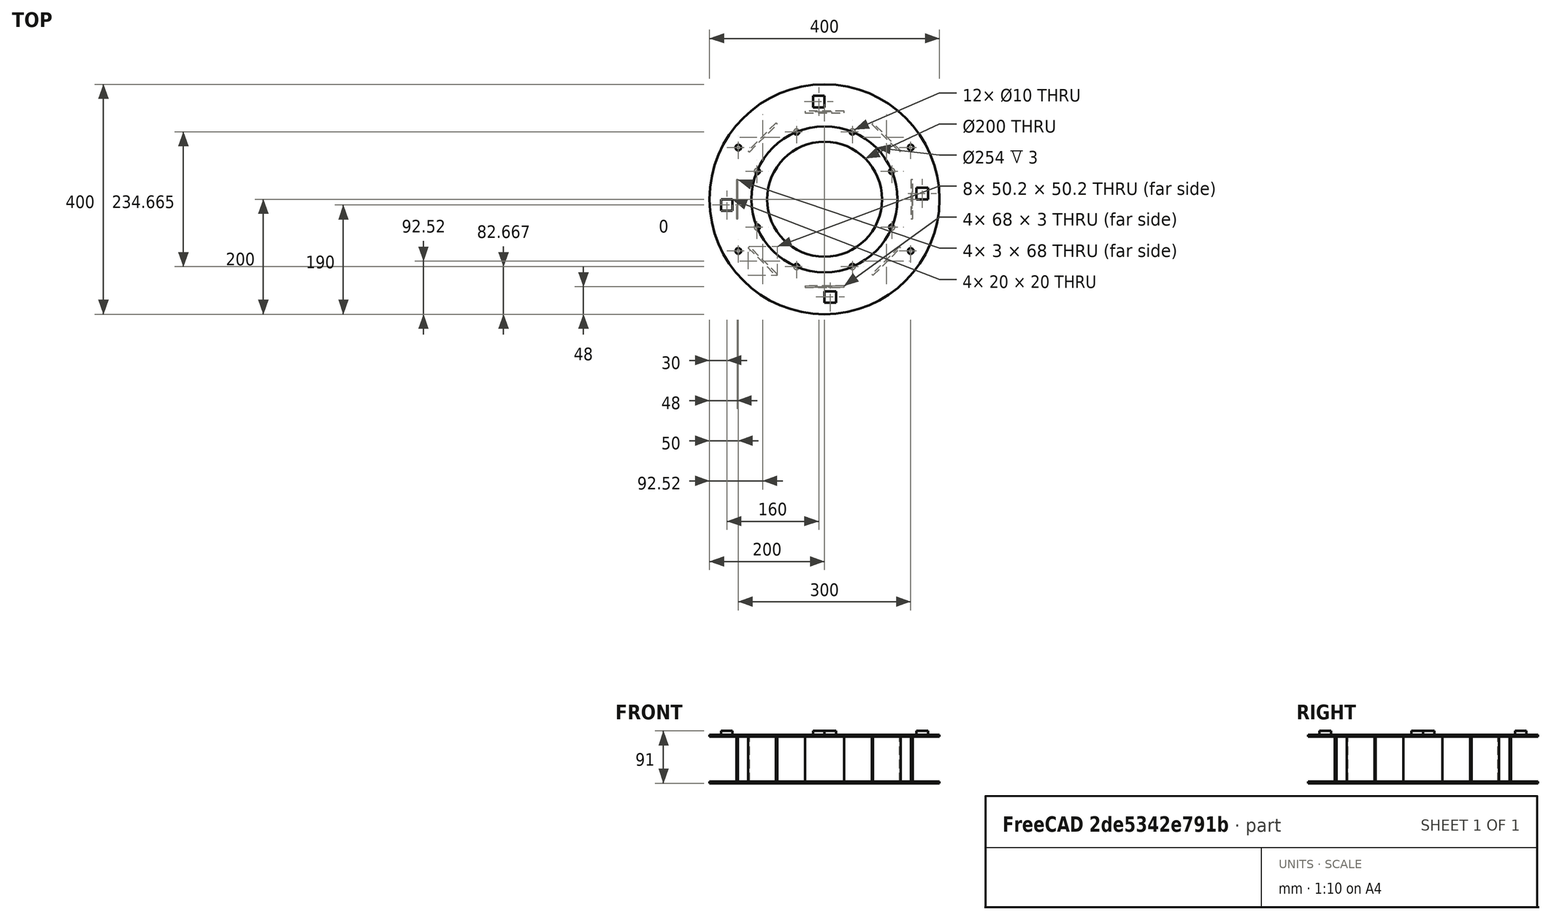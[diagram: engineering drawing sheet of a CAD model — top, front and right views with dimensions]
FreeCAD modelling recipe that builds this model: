
FCSTD DOCUMENT  (FreeCAD 0.21R33771 (Git))
Label: FEA_Model_MM
License: Creative Commons Attribution-ShareAlike 4.0
LicenseURL: https://creativecommons.org/licenses/by-sa/4.0/
objects: Sketcher::SketchObject×4, PartDesign::Pad×4, Fem::ConstraintForce×4, Fem::FemMeshObjectPython×2, PartDesign::Plane×1, PartDesign::PolarPattern×1, PartDesign::MultiTransform×1, App::MaterialObjectPython×1, Fem::ConstraintFixed×1, PartDesign::Body×1, Fem::FemSolverObjectPython×1, Fem::FemResultObjectPython×1, Fem::FemPostWarpVectorFilter×1, Fem::FemPostPipeline×1, Fem::FemAnalysis×1
note: 16 computed .brp shape members not serialized (recipe doc carries the construction recipe); baked Part::Feature solids carry a one-line shape summary decoded from their .brp

FEATURE [Sketcher::SketchObject] Sketch
  FullyConstrained = true
  MapMode = 5
  Support = -> [XY_Plane]
  sketch-geometry (19):
    g0: Circle CenterX=0 CenterY=0 CenterZ=0 NormalX=0 NormalY=0 NormalZ=1 AngleXU=0 Radius=100
    g1: Circle CenterX=0 CenterY=0 CenterZ=0 NormalX=0 NormalY=0 NormalZ=1 AngleXU=0 Radius=200
    g2: LineSegment StartX=-117.333 StartY=48.6008 StartZ=0 EndX=-117.333 EndY=-48.6008 EndZ=0
    g3: LineSegment StartX=-117.333 StartY=-48.6008 StartZ=0 EndX=-48.6008 EndY=-117.333 EndZ=0
    g4: LineSegment StartX=-48.6008 StartY=-117.333 StartZ=0 EndX=48.6008 EndY=-117.333 EndZ=0
    g5: LineSegment StartX=48.6008 StartY=-117.333 StartZ=0 EndX=117.333 EndY=-48.6008 EndZ=0
    g6: LineSegment StartX=117.333 StartY=-48.6008 StartZ=0 EndX=117.333 EndY=48.6008 EndZ=0
    g7: LineSegment StartX=117.333 StartY=48.6008 StartZ=0 EndX=48.6008 EndY=117.333 EndZ=0
    g8: LineSegment StartX=48.6008 StartY=117.333 StartZ=0 EndX=-48.6008 EndY=117.333 EndZ=0
    g9: LineSegment StartX=-48.6008 StartY=117.333 StartZ=0 EndX=-117.333 EndY=48.6008 EndZ=0
    g10: Circle CenterX=0 CenterY=0 CenterZ=0 NormalX=0 NormalY=0 NormalZ=1 AngleXU=0 Radius=127
    g11: Circle CenterX=-117.333 CenterY=48.6008 CenterZ=0 NormalX=0 NormalY=0 NormalZ=1 AngleXU=0 Radius=5
    g12: Circle CenterX=-48.6008 CenterY=117.333 CenterZ=0 NormalX=0 NormalY=0 NormalZ=1 AngleXU=0 Radius=5
    g13: Circle CenterX=48.6008 CenterY=117.333 CenterZ=0 NormalX=0 NormalY=0 NormalZ=1 AngleXU=0 Radius=5
    g14: Circle CenterX=117.333 CenterY=48.6008 CenterZ=0 NormalX=0 NormalY=0 NormalZ=1 AngleXU=0 Radius=5
    g15: Circle CenterX=117.333 CenterY=-48.6008 CenterZ=0 NormalX=0 NormalY=0 NormalZ=1 AngleXU=0 Radius=5
    g16: Circle CenterX=48.6008 CenterY=-117.333 CenterZ=0 NormalX=0 NormalY=0 NormalZ=1 AngleXU=0 Radius=5
    g17: Circle CenterX=-48.6008 CenterY=-117.333 CenterZ=0 NormalX=0 NormalY=0 NormalZ=1 AngleXU=0 Radius=5
    g18: Circle CenterX=-117.333 CenterY=-48.6008 CenterZ=0 NormalX=0 NormalY=0 NormalZ=1 AngleXU=0 Radius=5
  constraints (40):
    c: Coincident(g0,g-1)
    c: Coincident(g1,g0)
    c: Diameter(g1) = 400
    c: Diameter(g0) = 200
    c: Coincident(g2,g3)
    c: Coincident(g3,g4)
    c: Coincident(g4,g5)
    c: Coincident(g5,g6)
    c: Coincident(g6,g7)
    c: Coincident(g7,g8)
    c: Coincident(g8,g9)
    c: Coincident(g9,g2)
    c: Equal(g2, g3-g9) x7
    c: PointOnObject(g2,g10)
    c: PointOnObject(g3,g10)
    c: PointOnObject(g4,g10)
    c: PointOnObject(g5,g10)
    c: PointOnObject(g6,g10)
    c: PointOnObject(g7,g10)
    c: PointOnObject(g8,g10)
    c: PointOnObject(g9,g10)
    c: Coincident(g10,g0)
    c: Vertical(g2)
    c: Diameter(g10) = 254
    c: Coincident(g11,g2)
    c: Diameter(g11) = 10
    c: Equal(g11,g12) = 10
    c: Coincident(g12,g8)
    c: Coincident(g13,g7)
    c: Equal(g13,g11)
    c: Coincident(g14,g6)
    c: Coincident(g15,g5)
    c: Coincident(g16,g4)
    c: Coincident(g17,g3)
    c: Coincident(g18,g2)
    c: Equal(g14,g15)
    c: Equal(g15,g16)
    c: Equal(g16,g17)
    c: Equal(g17,g18)
    c: Equal(g18,g11)
FEATURE [PartDesign::Pad] Pad
  Direction = (0,0,1)
  Length = 3
  Length2 = 10
  Profile = -> Sketch
  ReferenceAxis = -> Sketch [N_Axis]
  Type = 0
FEATURE [Sketcher::SketchObject] Sketch001
  FullyConstrained = true
  MapMode = 5
  Support = -> [XY_Plane]
  sketch-geometry (7):
    g0: LineSegment StartX=-153.5 StartY=34 StartZ=0 EndX=-150.5 EndY=34 EndZ=0
    g1: LineSegment StartX=-150.5 StartY=34 StartZ=0 EndX=-150.5 EndY=-34 EndZ=0
    g2: LineSegment StartX=-150.5 StartY=-34 StartZ=0 EndX=-153.5 EndY=-34 EndZ=0
    g3: LineSegment StartX=-153.5 StartY=-34 StartZ=0 EndX=-153.5 EndY=34 EndZ=0
    g4: LineSegment StartX=-153.5 StartY=34 StartZ=0 EndX=-150.5 EndY=-34 EndZ=0
    g5: LineSegment StartX=-153.5 StartY=-34 StartZ=0 EndX=-150.5 EndY=34 EndZ=0
    g6: GeomPoint X=-152 Y=0 Z=0
  constraints (18):
    c: Coincident(g0,g1)
    c: Coincident(g1,g2)
    c: Coincident(g2,g3)
    c: Coincident(g3,g0)
    c: Horizontal(g0)
    c: Horizontal(g2)
    c: Vertical(g1)
    c: Vertical(g3)
    c: DistanceY(g3,g3) = 68
    c: DistanceX(g0,g0) = 3
    c: Coincident(g4,g0)
    c: Coincident(g4,g1)
    c: Coincident(g5,g2)
    c: Coincident(g5,g0)
    c: PointOnObject(g6,g4)
    c: PointOnObject(g6,g5)
    c: DistanceX(g6,g-1) = 152
    c: PointOnObject(g6,g-1)
FEATURE [PartDesign::Pad] Pad001
  BaseFeature = -> Pad
  Direction = (0,0,1)
  Length = 84
  Length2 = 10
  Profile = -> Sketch001
  ReferenceAxis = -> Sketch001 [N_Axis]
  Type = 0
FEATURE [PartDesign::Plane] DatumPlane
  AttachmentOffset = pos=(0,0,81) rot=(0,0,1;0rad)
  Length = 479.171
  MapMode = 5
  Placement = pos=(0,0,81) rot=(0,0,1;0rad)
  ResizeMode = 0
  Support = -> [XY_Plane]
  Width = 479.531
FEATURE [Sketcher::SketchObject] Sketch002
  FullyConstrained = true
  MapMode = 5
  Placement = pos=(0,0,81) rot=(0,0,1;0rad)
  Support = -> [DatumPlane]
  sketch-geometry (11):
    g0: Circle CenterX=0 CenterY=0 CenterZ=0 NormalX=0 NormalY=0 NormalZ=1 AngleXU=0 Radius=200
    g1: Circle CenterX=0 CenterY=0 CenterZ=0 NormalX=0 NormalY=0 NormalZ=1 AngleXU=0 Radius=127
    g2: Circle CenterX=-150 CenterY=90 CenterZ=0 NormalX=0 NormalY=0 NormalZ=1 AngleXU=0 Radius=5
    g3: Circle CenterX=-150 CenterY=-90 CenterZ=0 NormalX=0 NormalY=0 NormalZ=1 AngleXU=0 Radius=5
    g4: Circle CenterX=150 CenterY=90 CenterZ=0 NormalX=0 NormalY=0 NormalZ=1 AngleXU=0 Radius=5
    g5: Circle CenterX=150 CenterY=-90 CenterZ=0 NormalX=0 NormalY=0 NormalZ=1 AngleXU=0 Radius=5
    g6: LineSegment StartX=150 StartY=-90 StartZ=0 EndX=150 EndY=90 EndZ=0
    g7: LineSegment StartX=150 StartY=90 StartZ=0 EndX=-150 EndY=90 EndZ=0
    g8: LineSegment StartX=-150 StartY=90 StartZ=0 EndX=-150 EndY=-90 EndZ=0
    g9: LineSegment StartX=-150 StartY=-90 StartZ=0 EndX=150 EndY=-90 EndZ=0
    g10: GeomPoint X=0 Y=0 Z=0
  constraints (24):
    c: Diameter(g0) = 400
    c: Coincident(g1,g-1)
    c: Diameter(g1) = 254
    c: Coincident(g0,g1)
    c: Coincident(g6,g7)
    c: Coincident(g7,g8)
    c: Coincident(g8,g9)
    c: Coincident(g9,g6)
    c: Horizontal(g7)
    c: Horizontal(g9)
    c: Vertical(g6)
    c: Vertical(g8)
    c: Symmetric(g7,g6,g10)
    c: Coincident(g10,g0)
    c: Coincident(g7,g2)
    c: Coincident(g4,g6)
    c: Coincident(g5,g6)
    c: Coincident(g3,g8)
    c: Equal(g2,g4)
    c: Equal(g4,g5)
    c: Equal(g5,g3)
    c: Diameter(g2) = 10
    c: DistanceY(g8,g8) = 180
    c: DistanceX(g7,g7) = 300
FEATURE [PartDesign::Pad] Pad002
  BaseFeature = -> Pad001
  Direction = (0,0,1)
  Length = 3
  Length2 = 10
  Profile = -> Sketch002
  ReferenceAxis = -> Sketch002 [N_Axis]
  Type = 0
FEATURE [PartDesign::PolarPattern] PolarPattern
  Angle = 360
  Axis = -> Sketch001 [N_Axis]
  Occurrences = 8
FEATURE [PartDesign::MultiTransform] MultiTransform
  BaseFeature = -> Pad002
  Originals = -> [Pad001]
  Transformations = -> [PolarPattern]
FEATURE [App::MaterialObjectPython] MaterialSolid  # material (typed FeaturePython)
  Category = 0
  Material = AuthorAndLicense=(c) 2013 Juergen Riegel (CC-BY 3.0),CardName=Steel-Generic,Density=7900 kg/m^3,+9 more (map truncated)
FEATURE [Fem::ConstraintFixed] ConstraintFixed
  NormalDirection = (1,-1e-16,0)
  Normals = (96) [(-1,0,0),(0.5,-0.866025,0),(0.5,0.866025,0),(-1,2.44929e-16,0),(-1,0,0),(0.5,-0.866025,0),(0.5,0.866025,0),(-1,2.44929e-16,0),(-1,0,0),+87 more]
  Points = (96) [(122.333,-48.6008,3),(114.833,-44.2707,3),(114.833,-52.9309,3),(122.333,-48.6008,3),(122.333,-48.6008,1.5),(114.833,-44.2707,1.5),+90 more]
  References = -> [MultiTransform]
  Scale = 2
FEATURE [Sketcher::SketchObject] Sketch003
  FullyConstrained = true
  MapMode = 5
  Placement = pos=(0,0,81) rot=(0,0,1;0rad)
  Support = -> [DatumPlane]
  sketch-geometry (20):
    g0: LineSegment StartX=160 StartY=20 StartZ=0 EndX=160 EndY=0 EndZ=0
    g1: LineSegment StartX=160 StartY=0 StartZ=0 EndX=180 EndY=0 EndZ=0
    g2: LineSegment StartX=180 StartY=0 StartZ=0 EndX=180 EndY=20 EndZ=0
    g3: LineSegment StartX=180 StartY=20 StartZ=0 EndX=160 EndY=20 EndZ=0
    g4: GeomPoint X=170 Y=10 Z=0
    g5: LineSegment StartX=-20 StartY=180 StartZ=0 EndX=-20 EndY=160 EndZ=0
    g6: LineSegment StartX=-20 StartY=160 StartZ=0 EndX=0 EndY=160 EndZ=0
    g7: LineSegment StartX=0 StartY=160 StartZ=0 EndX=0 EndY=180 EndZ=0
    g8: LineSegment StartX=0 StartY=180 StartZ=0 EndX=-20 EndY=180 EndZ=0
    g9: GeomPoint X=-10 Y=170 Z=0
    g10: LineSegment StartX=-180 StartY=0 StartZ=0 EndX=-180 EndY=-20 EndZ=0
    g11: LineSegment StartX=-180 StartY=-20 StartZ=0 EndX=-160 EndY=-20 EndZ=0
    g12: LineSegment StartX=-160 StartY=-20 StartZ=0 EndX=-160 EndY=0 EndZ=0
    g13: LineSegment StartX=-160 StartY=0 StartZ=0 EndX=-180 EndY=0 EndZ=0
    g14: GeomPoint X=-170 Y=-10 Z=0
    g15: LineSegment StartX=0 StartY=-160 StartZ=0 EndX=0 EndY=-180 EndZ=0
    g16: LineSegment StartX=0 StartY=-180 StartZ=0 EndX=20 EndY=-180 EndZ=0
    g17: LineSegment StartX=20 StartY=-180 StartZ=0 EndX=20 EndY=-160 EndZ=0
    g18: LineSegment StartX=20 StartY=-160 StartZ=0 EndX=0 EndY=-160 EndZ=0
    g19: GeomPoint X=10 Y=-170 Z=0
  constraints (52):
    c: Coincident(g0,g1)
    c: Coincident(g1,g2)
    c: Coincident(g2,g3)
    c: Coincident(g3,g0)
    c: Horizontal(g1)
    c: Horizontal(g3)
    c: Vertical(g0)
    c: Vertical(g2)
    c: Symmetric(g1,g0,g4)
    c: Coincident(g5,g6)
    c: Coincident(g6,g7)
    c: Coincident(g7,g8)
    c: Coincident(g8,g5)
    c: Horizontal(g6)
    c: Horizontal(g8)
    c: Vertical(g5)
    c: Vertical(g7)
    c: Symmetric(g6,g5,g9)
    c: Coincident(g10,g11)
    c: Coincident(g11,g12)
    c: Coincident(g12,g13)
    c: Coincident(g13,g10)
    c: Horizontal(g11)
    c: Horizontal(g13)
    c: Vertical(g10)
    c: Vertical(g12)
    c: Symmetric(g11,g10,g14)
    c: Coincident(g15,g16)
    c: Coincident(g16,g17)
    c: Coincident(g17,g18)
    c: Coincident(g18,g15)
    c: Horizontal(g16)
    c: Horizontal(g18)
    c: Vertical(g15)
    c: Vertical(g17)
    c: Symmetric(g16,g15,g19)
    c: DistanceX(g16,g16) = 20
    c: PointOnObject(g15,g-2)
    c: Equal(g17,g18)
    c: DistanceY(g19,g-1) = 170
    c: DistanceY(g-1,g9) = 170
    c: DistanceX(g-1,g4) = 170
    c: DistanceX(g14,g-1) = 170
    c: Equal(g18,g13)
    c: Equal(g13,g12)
    c: Equal(g12,g6)
    c: Equal(g6,g7)
    c: Equal(g7,g3)
    c: Equal(g3,g2)
    c: PointOnObject(g12,g-1)
    c: PointOnObject(g0,g-1)
    c: PointOnObject(g6,g-2)
FEATURE [PartDesign::Pad] Pad003
  BaseFeature = -> MultiTransform
  Direction = (0,0,1)
  Length = 10
  Length2 = 10
  Profile = -> Sketch003
  ReferenceAxis = -> Sketch003 [N_Axis]
  Type = 0
FEATURE [PartDesign::Body] Body
  Group = -> [Sketch,Pad,Sketch001,Pad001,DatumPlane,Sketch002,Pad002,MultiTransform,PolarPattern,Sketch003,Pad003]
  Origin = -> Origin
  Tip = -> Pad003
FEATURE [Fem::ConstraintForce] ConstraintForce
  Direction = -> Pad003 [Face80]
  DirectionVector = (-1,0,0)
  Force = 2860
  NormalDirection = (1,0,0)
  Points = (9) [(0,160,91),(0,170,91),(0,180,91),(0,160,87.5),(0,170,87.5),(0,180,87.5),(0,160,84),(0,170,84),(0,180,84)]
  References = -> [Pad003]
FEATURE [Fem::ConstraintForce] ConstraintForce001
  Direction = -> Pad003 [Face69]
  DirectionVector = (0,-1,0)
  Force = 2860
  NormalDirection = (0,1,0)
  Points = (9) [(-160,-1.8434e-27,91),(-170,-1.8434e-27,91),(-180,-1.8434e-27,91),(-160,-1.8434e-27,87.5),(-170,-1.8434e-27,87.5),(-180,-1.8434e-27,87.5),+3 more]
  References = -> [Pad003]
FEATURE [Fem::ConstraintForce] ConstraintForce002
  Direction = -> Pad003 [Face74]
  DirectionVector = (1,0,0)
  Force = 2860
  NormalDirection = (-1,0,0)
  Points = (9) [(0,-160,91),(0,-170,91),(0,-180,91),(0,-160,87.5),(0,-170,87.5),(0,-180,87.5),(0,-160,84),(0,-170,84),(0,-180,84)]
  References = -> [Pad003]
FEATURE [Fem::ConstraintForce] ConstraintForce003
  Direction = -> Pad003 [Face83]
  DirectionVector = (0,1,0)
  Force = 2860
  NormalDirection = (0,-1,0)
  Points = (9) [(160,0,91),(170,0,91),(180,0,91),(160,0,87.5),(170,0,87.5),(180,0,87.5),(160,0,84),(170,0,84),(180,0,84)]
  References = -> [Pad003]
FEATURE [Fem::FemMeshObjectPython] FEMMeshGmsh  # FEM object (typed FeaturePython)
  Algorithm2D = 0
  Algorithm3D = 0
  CharacteristicLengthMax = 0
  CharacteristicLengthMin = 0
  CoherenceMesh = true
  ElementDimension = 0
  ElementOrder = 1
  GeometryTolerance = 1e-06
  GroupsOfNodes = false
  HighOrderOptimize = 0
  MeshSizeFromCurvature = 12
  OptimizeNetgen = false
  OptimizeStd = true
  Part = -> Pad003
  RecombinationAlgorithm = 0
  Recombine3DAll = false
  RecombineAll = false
  SecondOrderLinear = false
FEATURE [Fem::FemSolverObjectPython] SolverCalculix  # FEM object (typed FeaturePython)
  AnalysisType = 0
  BeamShellResultOutput3D = false
  BucklingFactors = 1
  EigenmodeHighLimit = 1000000
  EigenmodeLowLimit = 0
  EigenmodesCount = 10
  GeometricalNonlinearity = 0
  IterationsControlParameterCutb = 0.25,0.5,0.75,0.85,,,1.5,
  IterationsControlParameterIter = 4,8,9,200,10,400,,200,,
  IterationsControlParameterTimeUse = false
  IterationsThermoMechMaximum = 200
  IterationsUserDefinedIncrementations = false
  IterationsUserDefinedTimeStepLength = false
  MaterialNonlinearity = 0
  MatrixSolverType = 0
  SplitInputWriter = false
  ThermoMechSteadyState = true
  TimeEnd = 1
  TimeInitialStep = 1
FEATURE [Fem::FemMeshObjectPython] CalculiX_static_Results_Mesh  # FEM object (typed FeaturePython)
FEATURE [Fem::FemResultObjectPython] CalculiX_static_Results  # FEM object (typed FeaturePython)
  DisplacementLengths = [0.00443829,0.00948363,0.0531553,0.059592,0.0527868,0.0598505,0,0.0567763,0.0559713,0.0553691,0.0547576,0,0,0.0599348,0.0524196,0.0605346,0.0524333,0.00102122,0,0.0583304,0.0612851,0.0566849,0.0593827,0.0597518,0.0598739,0.0579958,0.0580854,+9944 more]
  DisplacementVectors = (9971) [(7.31591e-05,-0.00121443,0.00426828),(-0.000139388,0.0084701,0.00426348),(0.00177561,-0.000946487,-0.0531172),(0.00122495,-0.00164273,0.0595568),+9967 more]
  Eigenmode = 0
  EigenmodeFrequency = 0
  MaxShear = [2.86889,4.14064,26.6509,22.8504,33.4617,29.1717,38.147,38.7939,27.3453,29.3922,34.469,15.7311,75.7877,22.3645,35.0224,27.7075,45.6999,4.89391,72.4257,33.7964,34.082,29.3256,41.9173,42.3489,31.2234,34.9488,38.3984,13.9466,32.8553,32.0148,+9941 more]
  Mesh = -> CalculiX_static_Results_Mesh
  NodeNumbers = [1,2,3,4,5,6,7,8,9,10,11,12,13,14,15,16,17,18,19,20,21,22,23,24,25,26,27,28,29,30,31,32,33,34,35,36,37,38,39,40,41,42,43,44,45,46,47,48,49,50,51,52,53,54,55,56,57,58,59,60,61,62,63,64,65,66,67,68,69,+9902 more]
  NodeStrainXX = [2.89428e-06,2.9041e-06,0.000104244,-0.000127983,0.000239446,-0.000182598,0.000370822,0.000319939,-0.000232457,0.000237146,-0.000271771,9.57066e-05,0.000824076,0.000147686,-0.000158657,0.000183865,-0.000274726,-1.26717e-05,0.000447431,+9952 more]
  NodeStrainXY = [-7.32097e-06,5.97958e-06,-7.80433e-05,6.0767e-05,-2.5812e-05,-1.92927e-05,-0.000119813,-2.32105e-05,1.39353e-05,1.42495e-05,1.68466e-05,-8.68847e-05,-1.78014e-05,5.6663e-05,-0.000121466,-3.48939e-06,-9.62688e-06,-3.08973e-05,0.000367249,+9952 more]
  NodeStrainXZ = [1.3202e-06,-1.36864e-06,-5.23125e-05,3.86446e-05,-2.26082e-05,2.30176e-05,0.000109802,-6.58045e-06,-1.77337e-05,2.78298e-05,4.24475e-05,2.23947e-05,0.000270543,4.80188e-05,-5.20292e-05,5.5632e-05,-4.06931e-06,-5.32338e-06,0.000178004,+9952 more]
  NodeStrainYY = [2.29075e-05,3.33936e-05,0.000174772,-0.000114426,0.000224883,-0.000218856,2.95276e-06,0.000149745,-9.57722e-05,0.000164125,-0.00020956,-1.53717e-06,3.56518e-06,0.000103975,-0.000199856,0.000182289,-0.000323123,-2.53891e-06,-1.41523e-05,+9952 more]
  NodeStrainYZ = [1.2841e-06,9.02974e-06,-5.5933e-05,7.69168e-05,-3.82248e-05,-4.23362e-06,5.80178e-06,-5.04622e-05,3.41176e-05,-4.92033e-05,4.74339e-05,1.95932e-06,2.87708e-06,-4.41916e-05,1.68189e-05,-2.77438e-05,9.81444e-05,-3.17011e-07,-1.33907e-05,+9952 more]
  NodeStrainZZ = [-1.17415e-05,-1.59839e-05,-8.73548e-05,7.03779e-05,-0.00017079,0.000150288,1.07712e-06,-0.000173376,0.000114256,-0.000130948,0.000159416,8.5678e-07,1.95591e-06,-7.84967e-05,0.000138577,-0.000151594,0.000236308,7.1489e-06,6.50697e-07,+9952 more]
  NodeStressXX = [2.06761,2.79068,38.1522,-39.5394,70.7078,-57.0727,100.302,83.4109,-60.4517,67.675,-78.9551,25.6887,222.504,42.7014,-49.786,53.0439,-83.9816,-2.87968,118.904,51.1369,-54.3543,53.5211,-86.4604,69.8998,-47.8172,62.3084,-73.7053,-20.6531,+9943 more]
  NodeStressXY = [-1.1263,0.919936,-12.0067,9.34876,-3.97107,-2.96811,-18.4328,-3.57085,2.14389,2.19223,2.59178,-13.3669,-2.73867,8.71739,-18.6872,-0.536829,-1.48106,-4.75343,56.4998,-1.04933,-4.72128,-4.42276,-5.2529,-1.94584,-2.94422,-7.17263,-4.03634,+9944 more]
  NodeStressXZ = [0.203107,-0.21056,-8.04807,5.94532,-3.47819,3.54117,16.8926,-1.01238,-2.72826,4.28151,6.53039,3.44534,41.622,7.3875,-8.00449,8.55877,-0.626048,-0.818981,27.3852,5.63239,-3.68869,6.72319,-6.55228,-8.38748,5.59466,-6.89233,1.7657,-2.77551,+9943 more]
  NodeStressYY = [5.14657,7.48137,49.0026,-37.4538,68.4672,-62.6508,43.7064,57.2273,-39.4233,56.441,-69.3841,10.7281,96.2713,35.9767,-56.1243,52.8014,-91.4274,-1.3208,47.8915,75.8248,-79.9989,66.3502,-96.3886,96.0956,-70.9946,79.3833,-85.6091,-8.55843,+9943 more]
  NodeStressYZ = [0.197554,1.38919,-8.60507,11.8334,-5.88074,-0.651327,0.892581,-7.76342,5.24886,-7.56974,7.29753,0.301433,0.442628,-6.79871,2.58753,-4.26828,15.0991,-0.0487709,-2.0601,-0.15606,1.9649,3.16102,11.2425,-2.05551,2.54042,-2.27041,-6.40579,+9944 more]
  NodeStressZZ = [-0.184039,-0.115158,8.67549,-9.02238,7.59456,-5.85937,43.4178,7.51631,-7.1112,11.0451,-12.6186,11.0964,96.0237,7.90408,-4.05765,1.43477,-5.36108,0.169636,50.1689,9.01919,-13.1129,10.371,-17.9389,12.8376,-9.96761,13.2057,-11.0858,-8.89047,+9943 more]
  PrincipalMax = [5.51732,7.87645,56.9423,-2.5915,73.7235,-5.60287,109.639,83.8892,-6.17703,68.2402,-11.0136,33.877,235.017,48.8231,-2.01745,55.1462,-2.77979,2.81028,155.23,75.8717,-12.7012,67.7464,-15.6215,96.2648,-9.08692,81.9972,-10.4691,-0.608374,+9943 more]
  PrincipalMed = [1.73328,2.68527,35.2476,-35.1317,66.246,-56.0338,44.4425,57.9641,-39.9415,57.4649,-69.9927,11.2214,96.3408,33.665,-35.8882,52.4027,-83.8107,0.136403,51.3551,51.8302,-53.8998,53.4006,-85.7103,71.0012,-48.1587,60.8006,-72.6653,-8.99213,+9943 more]
  PrincipalMin = [-0.220463,-0.404828,3.64041,-48.2923,6.80006,-63.9462,33.3448,6.30128,-60.8677,9.45593,-79.9515,2.41482,83.4413,4.09409,-72.0623,-0.268841,-94.1796,-6.97753,10.379,8.27898,-80.8652,9.09531,-99.4561,11.567,-71.5338,12.0997,-87.2658,-28.5015,+9943 more]
  ResultType = Fem::ResultMechanical
  Stats = [-0.217164,0.209392,-0.21505,0.215152,-0.0930544,0.0757803,0,0.23343,0.464991,174.829,-101.481,276.622,-115.224,116.198,-282.777,99.23,0.267474,90.6476,0,0,0,0,0,0,0,0]
  Time = 0
  vonMises = [5.05264,7.24833,46.4261,40.747,63.5157,54.8171,71.395,68.4143,47.7965,54.2059,64.5374,28.1132,145.555,39.4011,60.6715,54.0955,86.6817,8.76239,129.327,59.3442,59.4592,52.9562,77.8769,75.3139,54.6471,62.0755,70.6374,24.7884,59.0823,55.4512,+9941 more]
FEATURE [Fem::FemPostWarpVectorFilter] WarpVector
  Factor = 49.51
  Vector = 0
FEATURE [Fem::FemPostPipeline] Pipeline_CalculiX_static_Results
  Filter = -> [WarpVector]
  Mode = 2
FEATURE [Fem::FemAnalysis] Analysis
  Group = -> [MaterialSolid,ConstraintFixed,ConstraintForce,ConstraintForce001,ConstraintForce002,ConstraintForce003,FEMMeshGmsh,SolverCalculix,Pipeline_CalculiX_static_Results,CalculiX_static_Results]
